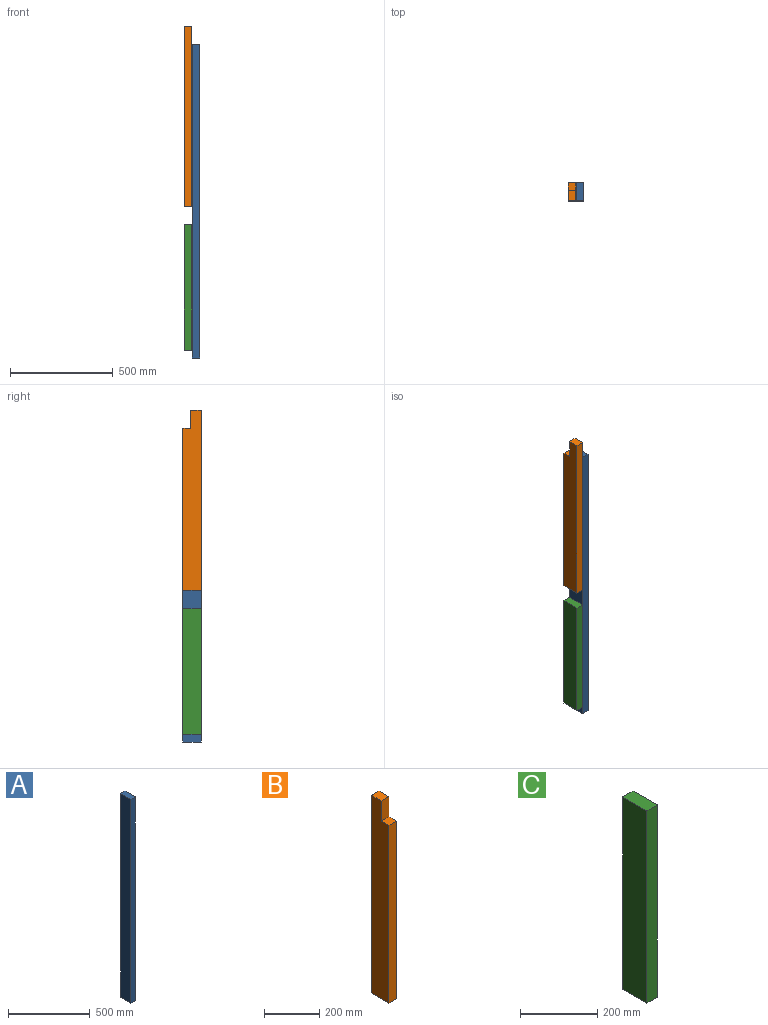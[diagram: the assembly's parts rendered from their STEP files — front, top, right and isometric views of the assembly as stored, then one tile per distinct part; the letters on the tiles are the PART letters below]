
ASSEMBLY  parts=3 mates=2
PART A: 6 faces, bbox 38.1x88.9x1524 mm
  f0: plane 1524x38.1mm, normal (0,-1,0), area 58064.4mm2, adj f1,f3,f4,f5
  f1: plane 88.9x38.1mm, normal (0,0,-1), area 3387.1mm2, adj f0,f2,f4,f5
  f2: plane 1524x38.1mm, normal (0,1,0), area 58064.4mm2, adj f1,f3,f4,f5
  f3: plane 88.9x38.1mm, normal (0,0,1), area 3387.1mm2, adj f0,f2,f4,f5
  f4: plane 1524x88.9mm, normal (-1,0,0), area 135483.6mm2, adj f0,f1,f2,f3
  f5: plane 1524x88.9mm, normal (1,0,0), area 135483.6mm2, adj f0,f1,f2,f3
PART B: 8 faces, bbox 38.1x88.9x876.3 mm
  f0: plane 50.8x38.1mm, normal (0,0,1), area 1935.5mm2, adj f1,f5,f6,f7
  f1: plane 88.9x38.1mm, normal (0,-1,0), area 3387.1mm2, adj f0,f2,f6,f7
  f2: plane 38.1x38.1mm, normal (0,0,1), area 1451.6mm2, adj f1,f3,f6,f7
  f3: plane 787.4x38.1mm, normal (0,-1,0), area 29999.9mm2, adj f2,f4,f6,f7
  f4: plane 88.9x38.1mm, normal (0,0,-1), area 3387.1mm2, adj f3,f5,f6,f7
  f5: plane 876.3x38.1mm, normal (0,1,0), area 33387mm2, adj f0,f4,f6,f7
  f6: plane 876.3x88.9mm, normal (1,0,0), area 74516mm2, adj f0,f1,f2,f3,f4,f5
  f7: plane 876.3x88.9mm, normal (-1,0,0), area 74516mm2, adj f0,f1,f2,f3,f4,f5
PART C: 6 faces, bbox 38.1x88.9x609.6 mm
  f0: plane 88.9x38.1mm, normal (0,0,-1), area 3387.1mm2, adj f1,f3,f4,f5
  f1: plane 609.6x38.1mm, normal (0,1,0), area 23225.8mm2, adj f0,f2,f4,f5
  f2: plane 88.9x38.1mm, normal (0,0,1), area 3387.1mm2, adj f1,f3,f4,f5
  f3: plane 609.6x38.1mm, normal (0,-1,0), area 23225.8mm2, adj f0,f2,f4,f5
  f4: plane 609.6x88.9mm, normal (1,0,0), area 54193.4mm2, adj f0,f1,f2,f3
  f5: plane 609.6x88.9mm, normal (-1,0,0), area 54193.4mm2, adj f0,f1,f2,f3
PLACE A rot(axis=(0,0,-1),0deg) t=(567.42,1399.72,-286.29)mm
PLACE B rot(axis=(0,0,1),180deg) t=(-2315.48,955.22,-286.29)mm
PLACE C rot(axis=(0,0,1),180deg) t=(-2315.48,2745.92,-286.29)mm
MATE fastened A.f4 <-> B.f7  axis (-1,0,0) through (-893.08,1221.92,1263.11)mm
MATE fastened C.f5 <-> A.f4  axis (1,0,0) through (-893.08,1177.47,-222.79)mm
